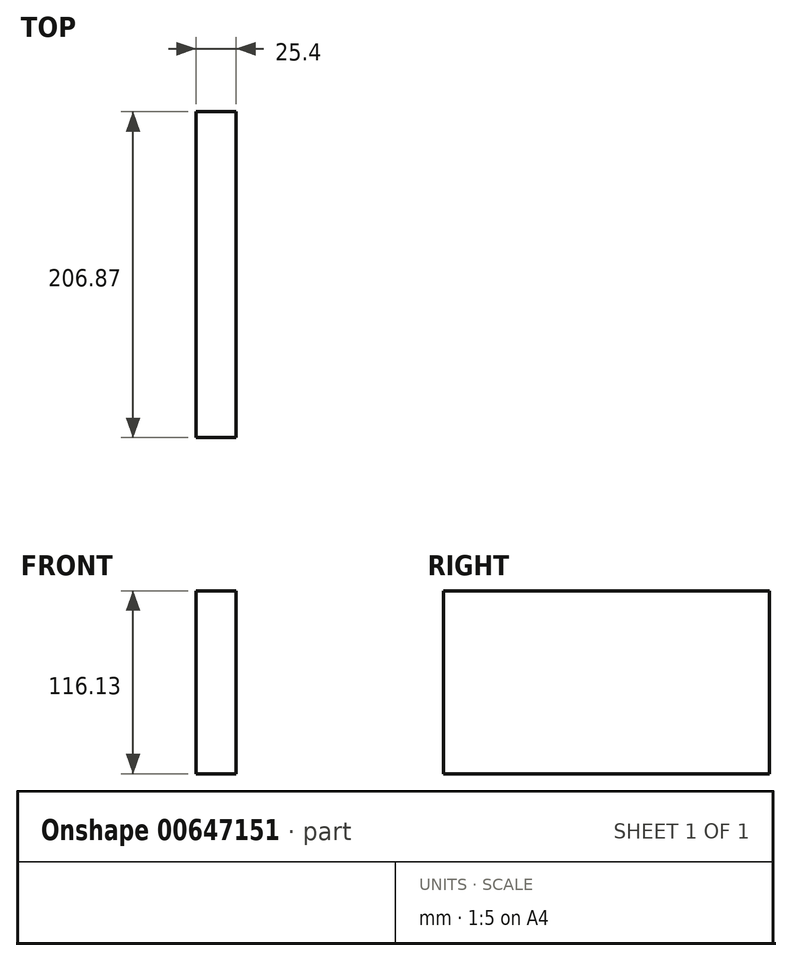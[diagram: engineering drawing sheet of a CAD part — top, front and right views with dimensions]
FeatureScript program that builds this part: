
annotation { "Feature Type Name" : "Feature", "Feature Type Description" : "" }
export const myFeature = defineFeature(function(context is Context, id is Id, definition is map)
    precondition{}
    {
        {
            var Q0;
            Q0=qCreatedBy(makeId("Right.planeOp"),FACE);
            var sketch = newSketch(context, id + "F0", { "sketchPlane" : qUnion([Q0])});
            skLineSegment(sketch, "E0.bottom", {"start": v(-111.46, 54.18) * mm, "end": v(95.4, 54.18) * mm});
            skLineSegment(sketch, "E0.top", {"start": v(-111.46, -61.95) * mm, "end": v(95.4, -61.95) * mm});
            skLineSegment(sketch, "E0.left", {"start": v(-111.46, 54.18) * mm, "end": v(-111.46, -61.95) * mm});
            skLineSegment(sketch, "E0.right", {"start": v(95.4, 54.18) * mm, "end": v(95.4, -61.95) * mm});
            skSolve(sketch);
        }
        {
            var Q0;
            Q0 = qSketchRegion(id + "F0", true);
            extrude(context, id + "F1", {"entities" : qUnion([Q0]), "depth" : 25.4 * mm, "offsetDistance" : 25.4 * mm});
        }
    });
